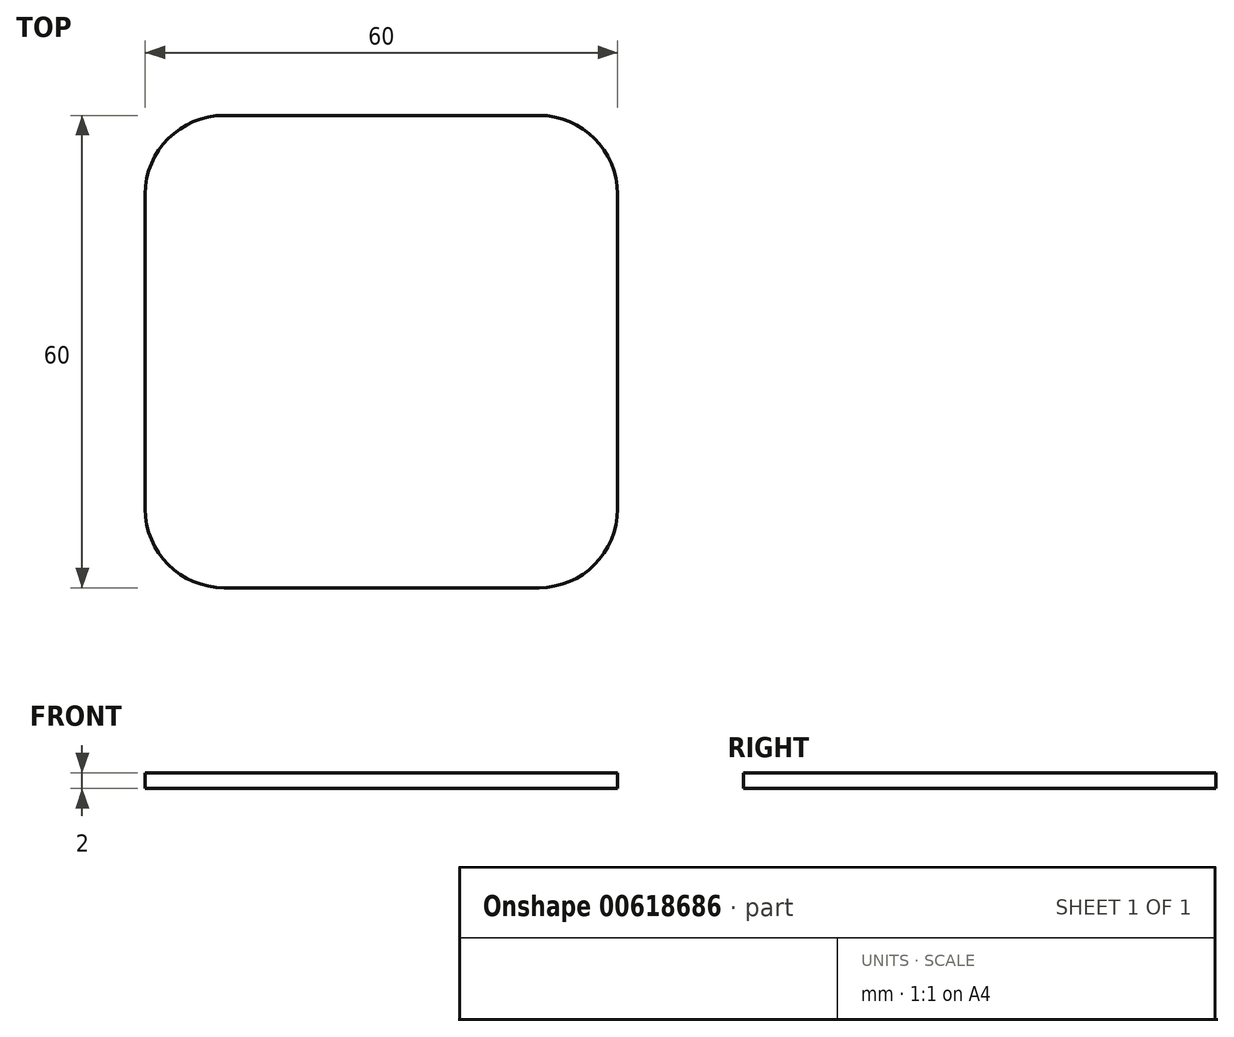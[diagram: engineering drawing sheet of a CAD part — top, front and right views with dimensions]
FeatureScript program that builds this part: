
annotation { "Feature Type Name" : "Feature", "Feature Type Description" : "" }
export const myFeature = defineFeature(function(context is Context, id is Id, definition is map)
    precondition{}
    {
        {
            var Q0;
            Q0=qCreatedBy(makeId("Top.planeOp"),FACE);
            var sketch = newSketch(context, id + "F0", { "sketchPlane" : qUnion([Q0])});
            skLineSegment(sketch, "E0.bottom", {"start": v(-20, 30) * mm, "end": v(20, 30) * mm});
            skLineSegment(sketch, "E0.top", {"start": v(-20, -30) * mm, "end": v(20, -30) * mm});
            skLineSegment(sketch, "E0.left", {"start": v(-30, 20) * mm, "end": v(-30, -20) * mm});
            skLineSegment(sketch, "E0.right", {"start": v(30, 20) * mm, "end": v(30, -20) * mm});
            skPoint(sketch, "E0.middle", {"position": v(0, 0) * mm});
            skPoint(sketch, "E1.visualSharp", {"position": v(-30, 30) * mm});
            skArc(sketch, "E1.filletArc", {"start": v(-20, 30) * mm, "mid": v(-27.07, 27.07) * mm, "end": v(-30, 20) * mm});
            skPoint(sketch, "E2.visualSharp", {"position": v(30, 30) * mm});
            skArc(sketch, "E2.filletArc", {"start": v(30, 20) * mm, "mid": v(27.07, 27.07) * mm, "end": v(20, 30) * mm});
            skPoint(sketch, "E3.visualSharp", {"position": v(30, -30) * mm});
            skArc(sketch, "E3.filletArc", {"start": v(20, -30) * mm, "mid": v(27.07, -27.07) * mm, "end": v(30, -20) * mm});
            skPoint(sketch, "E4.visualSharp", {"position": v(-30, -30) * mm});
            skArc(sketch, "E4.filletArc", {"start": v(-30, -20) * mm, "mid": v(-27.07, -27.07) * mm, "end": v(-20, -30) * mm});
            skSolve(sketch);
        }
        {
            var Q0;
            Q0=makeQuery(id+"F0.imprint","IMPRINT",FACE,{"disambiguationData":[TD([[makeQuery(id+"F0.imprint","IMPRINT",EDGE,{"derivedFrom":sQuery(id+"F0.wireOp",EDGE,"E0.bottom")}),-1.0]])]});
            extrude(context, id + "F1", {"entities" : qUnion([Q0]), "depth" : 2 * mm, "offsetDistance" : 25 * mm});
        }
    });
